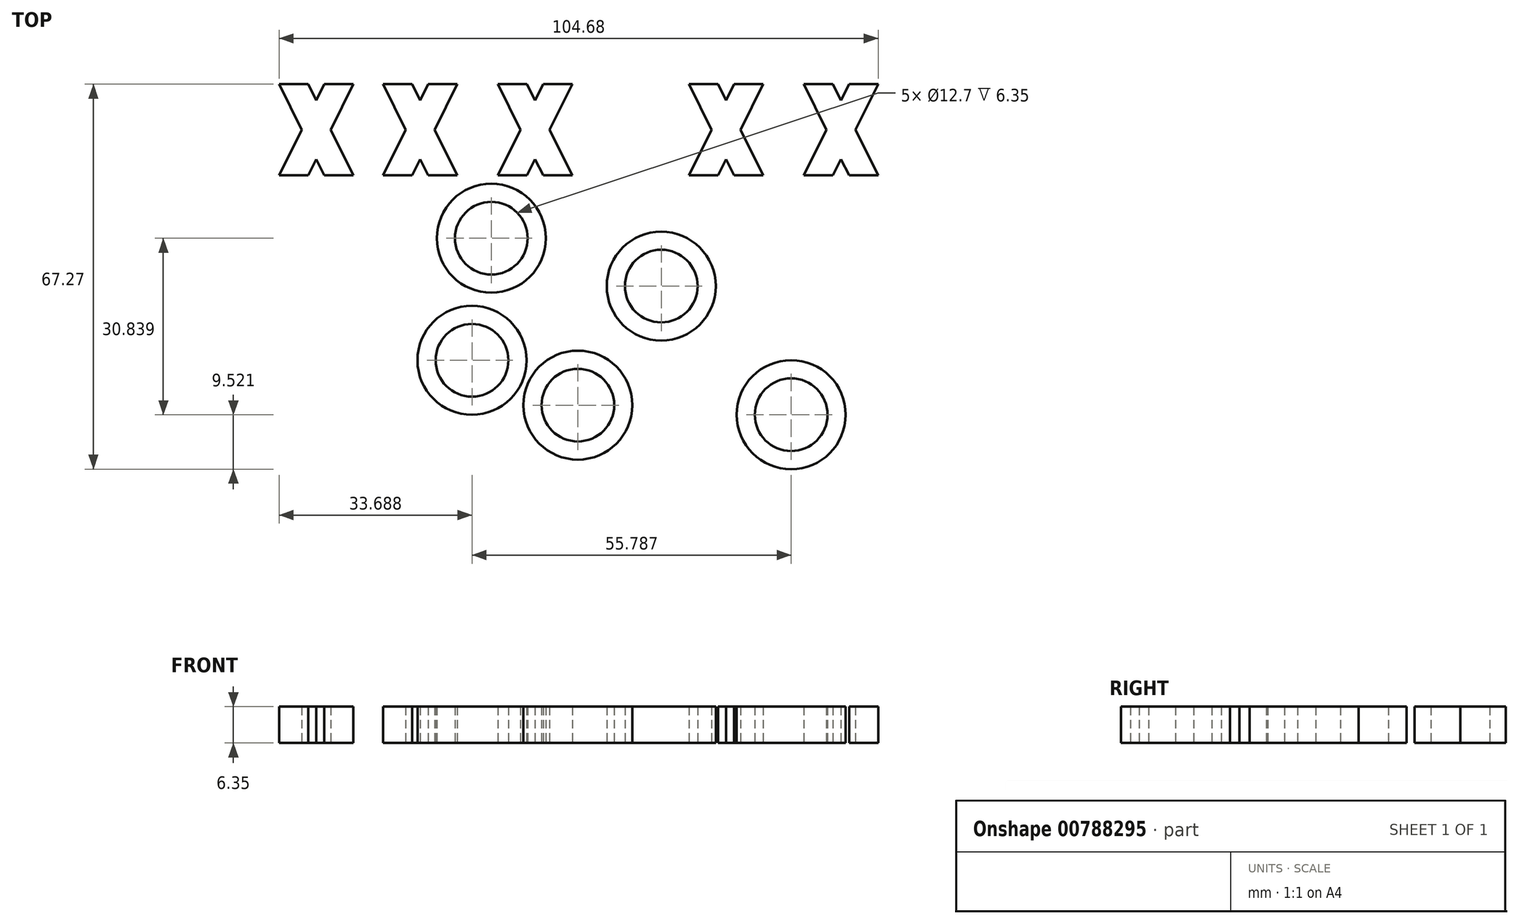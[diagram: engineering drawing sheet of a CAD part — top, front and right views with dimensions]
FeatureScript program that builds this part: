
annotation { "Feature Type Name" : "Feature", "Feature Type Description" : "" }
export const myFeature = defineFeature(function(context is Context, id is Id, definition is map)
    precondition{}
    {
        {
            var Q0;
            Q0=qCreatedBy(makeId("Top.planeOp"),FACE);
            var sketch = newSketch(context, id + "F0", { "sketchPlane" : qUnion([Q0])});
            skCircle(sketch, "E0", {"center": v(-3.77, -29.16) * mm, "radius": 9.53 * mm});
            skCircle(sketch, "E1", {"center": v(-18.89, 0) * mm, "radius": 6.35 * mm});
            skCircle(sketch, "E2", {"center": v(-18.89, 0) * mm, "radius": 9.53 * mm});
            skCircle(sketch, "E3", {"center": v(-22.27, -21.33) * mm, "radius": 9.53 * mm});
            skCircle(sketch, "E4", {"center": v(-22.27, -21.33) * mm, "radius": 6.35 * mm});
            skCircle(sketch, "E5", {"center": v(10.8, -8.36) * mm, "radius": 6.35 * mm});
            skCircle(sketch, "E6", {"center": v(10.8, -8.36) * mm, "radius": 9.53 * mm});
            skCircle(sketch, "E7", {"center": v(33.52, -30.84) * mm, "radius": 6.35 * mm});
            skCircle(sketch, "E8", {"center": v(33.52, -30.84) * mm, "radius": 9.53 * mm});
            skPoint(sketch, "E9.start.orphan", {"position": v(-28.29, 18.32) * mm});
            skPoint(sketch, "E10.end.orphan", {"position": v(-28.29, 5.88) * mm});
            skCircle(sketch, "E11", {"center": v(-3.77, -29.16) * mm, "radius": 6.35 * mm});
            skLineSegment(sketch, "E12", {"start": v(-17.72, 26.91) * mm, "end": v(-12.64, 26.91) * mm});
            skLineSegment(sketch, "E13", {"start": v(-12.64, 26.91) * mm, "end": v(-4.75, 10.98) * mm});
            skLineSegment(sketch, "E14", {"start": v(-4.75, 10.98) * mm, "end": v(-9.83, 10.98) * mm});
            skLineSegment(sketch, "E15", {"start": v(-9.83, 10.98) * mm, "end": v(-17.72, 26.91) * mm});
            skLineSegment(sketch, "E16", {"start": v(-12.64, 10.98) * mm, "end": v(-4.75, 26.91) * mm});
            skLineSegment(sketch, "E17", {"start": v(-4.75, 26.91) * mm, "end": v(-9.83, 26.91) * mm});
            skLineSegment(sketch, "E18", {"start": v(-9.83, 26.91) * mm, "end": v(-17.72, 10.98) * mm});
            skLineSegment(sketch, "E19", {"start": v(-17.72, 10.98) * mm, "end": v(-12.64, 10.98) * mm});
            skLineSegment(sketch, "E20", {"start": v(-21.29, 50.32) * mm, "end": v(-21.29, 45.16) * mm});
            skLineSegment(sketch, "E21.MirrorCS", {"start": v(-29.94, 10.98) * mm, "end": v(-37.83, 26.91) * mm});
            skLineSegment(sketch, "E22.MirrorCS", {"start": v(-24.86, 26.91) * mm, "end": v(-29.94, 26.91) * mm});
            skLineSegment(sketch, "E23.MirrorCS", {"start": v(-32.75, 10.98) * mm, "end": v(-24.86, 26.91) * mm});
            skLineSegment(sketch, "E24.MirrorCS", {"start": v(-37.83, 26.91) * mm, "end": v(-32.75, 26.91) * mm});
            skLineSegment(sketch, "E25.MirrorCS", {"start": v(-37.83, 10.98) * mm, "end": v(-32.75, 10.98) * mm});
            skLineSegment(sketch, "E26.MirrorCS", {"start": v(-24.86, 10.98) * mm, "end": v(-29.94, 10.98) * mm});
            skLineSegment(sketch, "E27.MirrorCS", {"start": v(-32.75, 26.91) * mm, "end": v(-24.86, 10.98) * mm});
            skLineSegment(sketch, "E28.MirrorCS", {"start": v(-29.94, 26.91) * mm, "end": v(-37.83, 10.98) * mm});
            skLineSegment(sketch, "E29", {"start": v(5.44, 51.08) * mm, "end": v(5.44, 44.78) * mm});
            skLineSegment(sketch, "E30.MirrorCS", {"start": v(43.64, 26.91) * mm, "end": v(35.75, 10.98) * mm});
            skLineSegment(sketch, "E31.MirrorCS", {"start": v(28.61, 26.91) * mm, "end": v(23.53, 26.91) * mm});
            skLineSegment(sketch, "E32.MirrorCS", {"start": v(35.75, 26.91) * mm, "end": v(40.83, 26.91) * mm});
            skLineSegment(sketch, "E33.MirrorCS", {"start": v(48.72, 26.91) * mm, "end": v(43.64, 26.91) * mm});
            skLineSegment(sketch, "E34.MirrorCS", {"start": v(20.72, 26.91) * mm, "end": v(28.61, 10.98) * mm});
            skLineSegment(sketch, "E35.MirrorCS", {"start": v(35.75, 10.98) * mm, "end": v(40.83, 10.98) * mm});
            skLineSegment(sketch, "E36.MirrorCS", {"start": v(43.64, 10.98) * mm, "end": v(35.75, 26.91) * mm});
            skLineSegment(sketch, "E37.MirrorCS", {"start": v(15.64, 26.91) * mm, "end": v(20.72, 26.91) * mm});
            skLineSegment(sketch, "E38.MirrorCS", {"start": v(23.53, 10.98) * mm, "end": v(15.64, 26.91) * mm});
            skLineSegment(sketch, "E39.MirrorCS", {"start": v(20.72, 10.98) * mm, "end": v(28.61, 26.91) * mm});
            skLineSegment(sketch, "E40.MirrorCS", {"start": v(40.83, 10.98) * mm, "end": v(48.72, 26.91) * mm});
            skLineSegment(sketch, "E41.MirrorCS", {"start": v(40.83, 26.91) * mm, "end": v(48.72, 10.98) * mm});
            skLineSegment(sketch, "E42.MirrorCS", {"start": v(48.72, 10.98) * mm, "end": v(43.64, 10.98) * mm});
            skLineSegment(sketch, "E43.MirrorCS", {"start": v(23.53, 26.91) * mm, "end": v(15.64, 10.98) * mm});
            skLineSegment(sketch, "E44.MirrorCS", {"start": v(15.64, 10.98) * mm, "end": v(20.72, 10.98) * mm});
            skLineSegment(sketch, "E45.MirrorCS", {"start": v(32.18, 50.32) * mm, "end": v(32.18, 45.16) * mm});
            skLineSegment(sketch, "E46.MirrorCS", {"start": v(28.61, 10.98) * mm, "end": v(23.53, 10.98) * mm});
            skLineSegment(sketch, "E47", {"start": v(-6.59, 26.91) * mm, "end": v(-6.59, 25.11) * mm});
            skLineSegment(sketch, "E48", {"start": v(-30.36, 51.46) * mm, "end": v(-30.36, 44.59) * mm});
            skLineSegment(sketch, "E49.MirrorCS", {"start": v(-55.96, 10.98) * mm, "end": v(-50.88, 10.98) * mm});
            skLineSegment(sketch, "E50.MirrorCS", {"start": v(-43, 10.98) * mm, "end": v(-48.07, 10.98) * mm});
            skLineSegment(sketch, "E51.MirrorCS", {"start": v(-48.07, 10.98) * mm, "end": v(-55.96, 26.91) * mm});
            skLineSegment(sketch, "E52.MirrorCS", {"start": v(-50.88, 10.98) * mm, "end": v(-43, 26.91) * mm});
            skLineSegment(sketch, "E53.MirrorCS", {"start": v(-55.96, 26.91) * mm, "end": v(-50.88, 26.91) * mm});
            skLineSegment(sketch, "E54.MirrorCS", {"start": v(-43, 26.91) * mm, "end": v(-48.07, 26.91) * mm});
            skLineSegment(sketch, "E55.MirrorCS", {"start": v(-50.88, 26.91) * mm, "end": v(-43, 10.98) * mm});
            skLineSegment(sketch, "E56.MirrorCS", {"start": v(-48.07, 26.91) * mm, "end": v(-55.96, 10.98) * mm});
            skSolve(sketch);
        }
        {
            var Q0;
            Q0 = qSketchRegion(id + "F0", true);
            extrude(context, id + "F1", {"entities" : qUnion([Q0]), "depth" : 6.35 * mm, "offsetDistance" : 25.4 * mm});
        }
    });
